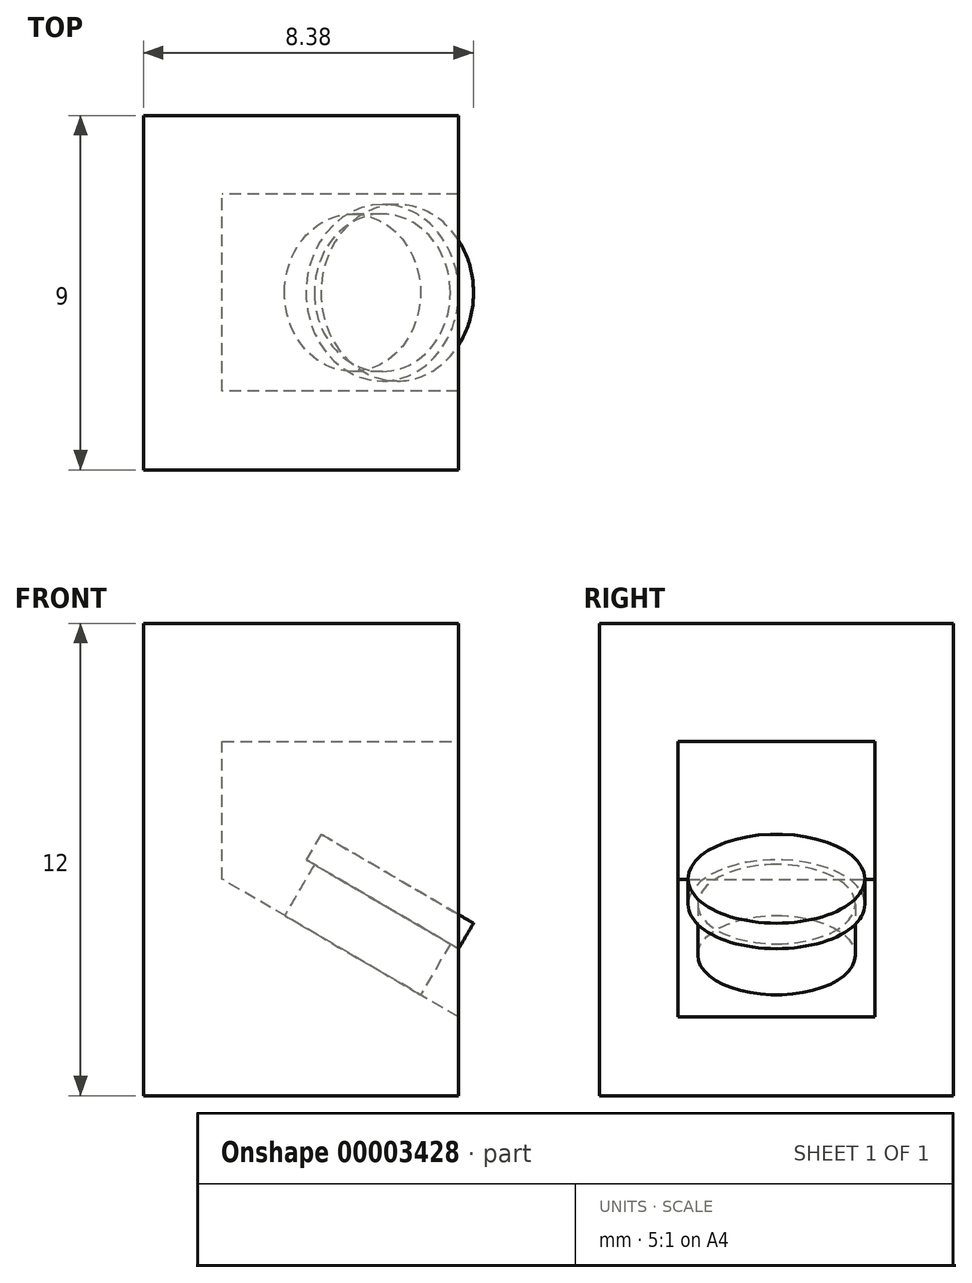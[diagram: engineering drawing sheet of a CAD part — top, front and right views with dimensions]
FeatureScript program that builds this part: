
annotation { "Feature Type Name" : "Feature", "Feature Type Description" : "" }
export const myFeature = defineFeature(function(context is Context, id is Id, definition is map)
    precondition{}
    {
        {
            var Q0;
            Q0=qCreatedBy(makeId("Right.planeOp"),FACE);
            var sketch = newSketch(context, id + "F0", { "sketchPlane" : qUnion([Q0])});
            skLineSegment(sketch, "E0.bottom", {"start": v(0, 0) * mm, "end": v(9, 0) * mm});
            skLineSegment(sketch, "E0.top", {"start": v(0, 12) * mm, "end": v(9, 12) * mm});
            skLineSegment(sketch, "E0.left", {"start": v(0, 0) * mm, "end": v(0, 12) * mm});
            skLineSegment(sketch, "E0.right", {"start": v(9, 0) * mm, "end": v(9, 12) * mm});
            skSolve(sketch);
        }
        {
            var Q0;
            Q0=makeQuery(id+"F0.imprint","IMPRINT",FACE,{"disambiguationData":[TD([[makeQuery(id+"F0.imprint","IMPRINT",EDGE,{"derivedFrom":sQuery(id+"F0.wireOp",EDGE,"E0.bottom")}),1.0]])]});
            extrude(context, id + "F1", {"entities" : qUnion([Q0]), "depth" : 8 * mm});
        }
        {
            var Q0;
            Q0=makeQuery(id+"F1.opExtrude","CAP_FACE",FACE,{"disambiguationData":[OSD([sQuery(id+"F0.wireOp",EDGE,"E0.bottom"),sQuery(id+"F0.wireOp",EDGE,"E0.top"),sQuery(id+"F0.wireOp",EDGE,"E0.left"),sQuery(id+"F0.wireOp",EDGE,"E0.right")])],"isStart":false});
            var sketch = newSketch(context, id + "F2", { "sketchPlane" : qUnion([Q0])});
            skLineSegment(sketch, "E1.bottom", {"start": v(2, 2) * mm, "end": v(7, 2) * mm});
            skLineSegment(sketch, "E1.top", {"start": v(2, 9) * mm, "end": v(7, 9) * mm});
            skLineSegment(sketch, "E1.left", {"start": v(2, 2) * mm, "end": v(2, 9) * mm});
            skLineSegment(sketch, "E1.right", {"start": v(7, 2) * mm, "end": v(7, 9) * mm});
            skSolve(sketch);
        }
        {
            var Q0;
            Q0=makeQuery(id+"F2.imprint","IMPRINT",FACE,{"disambiguationData":[TD([[makeQuery(id+"F2.imprint","IMPRINT",EDGE,{"derivedFrom":sQuery(id+"F2.wireOp",EDGE,"E1.bottom")}),1.0]])]});
            extrude(context, id + "F3", {"entities" : qUnion([Q0]), "operationType" : NewBodyOperationType.REMOVE, "oppositeDirection" : true, "depth" : 6 * mm});
        }
        {
            var Q0;
            Q0=makeQuery(id+"F3.boolean.opBoolean","COPY",FACE,{"derivedFrom":makeQuery(id+"F3.opExtrude","SWEPT_FACE",FACE,{"disambiguationData":[OSD([sQuery(id+"F2.wireOp",EDGE,"E1.right")])]})});
            var sketch = newSketch(context, id + "F4", { "sketchPlane" : qUnion([Q0])});
            skLineSegment(sketch, "E2", {"start": v(8, 2) * mm, "end": v(2, 5.5) * mm});
            skSolve(sketch);
        }
        {
            var Q0;
            {var subQ2=sQuery(id+"F4.wireOp",EDGE,"E2");Q0=makeQuery(id+"F4.imprint","IMPRINT",FACE,{"disambiguationData":[TD([[makeQuery(id+"F4.imprint","IMPRINT",EDGE,{"derivedFrom":subQ2}),1.0]])]});}
            extrude(context, id + "F5", {"entities" : qUnion([Q0]), "operationType" : NewBodyOperationType.ADD, "depth" : 5 * mm});
        }
        {
            var Q0;
            Q0=makeQuery(id+"F5.opExtrude","SWEPT_FACE",FACE,{"disambiguationData":[OSD([sQuery(id+"F4.wireOp",EDGE,"E2")])]});
            var sketch = newSketch(context, id + "F6", { "sketchPlane" : qUnion([Q0])});
            skCircle(sketch, "E3", {"center": v(2.79, 4.5) * mm, "radius": 2 * mm});
            skSolve(sketch);
        }
        {
            var Q0;
            Q0=makeQuery(id+"F6.imprint","IMPRINT",FACE,{"disambiguationData":[TD([[makeQuery(id+"F6.imprint","IMPRINT",EDGE,{"derivedFrom":sQuery(id+"F6.wireOp",EDGE,"E3")}),1.0]])]});
            extrude(context, id + "F7", {"entities" : qUnion([Q0]), "operationType" : NewBodyOperationType.ADD, "depth" : 1.5 * mm});
        }
        {
            var Q0;
            Q0=makeQuery(id+"F7.opExtrude","CAP_FACE",FACE,{"disambiguationData":[OSD([sQuery(id+"F6.wireOp",EDGE,"E3")])],"isStart":false});
            var sketch = newSketch(context, id + "F8", { "sketchPlane" : qUnion([Q0])});
            skCircle(sketch, "E4", {"center": v(2.79, 4.5) * mm, "radius": 2.24 * mm});
            skSolve(sketch);
        }
        {
            var Q0;
            Q0=makeQuery(id+"F8.imprint","IMPRINT",FACE,{"disambiguationData":[TD([[makeQuery(id+"F8.imprint","IMPRINT",EDGE,{"derivedFrom":makeQuery(id+"F7.opExtrude","CAP_EDGE",EDGE,{"disambiguationData":[OSD([sQuery(id+"F6.wireOp",EDGE,"E3")])],"isStart":false})}),1.0]])]});
            var Q1;
            Q1=makeQuery(id+"F8.imprint","IMPRINT",FACE,{"disambiguationData":[TD([[makeQuery(id+"F8.imprint","IMPRINT",EDGE,{"derivedFrom":sQuery(id+"F8.wireOp",EDGE,"E4")}),1.0]])]});
            extrude(context, id + "F9", {"entities" : qUnion([Q0, Q1]), "operationType" : NewBodyOperationType.ADD, "depth" : .75 * mm});
        }
    });
